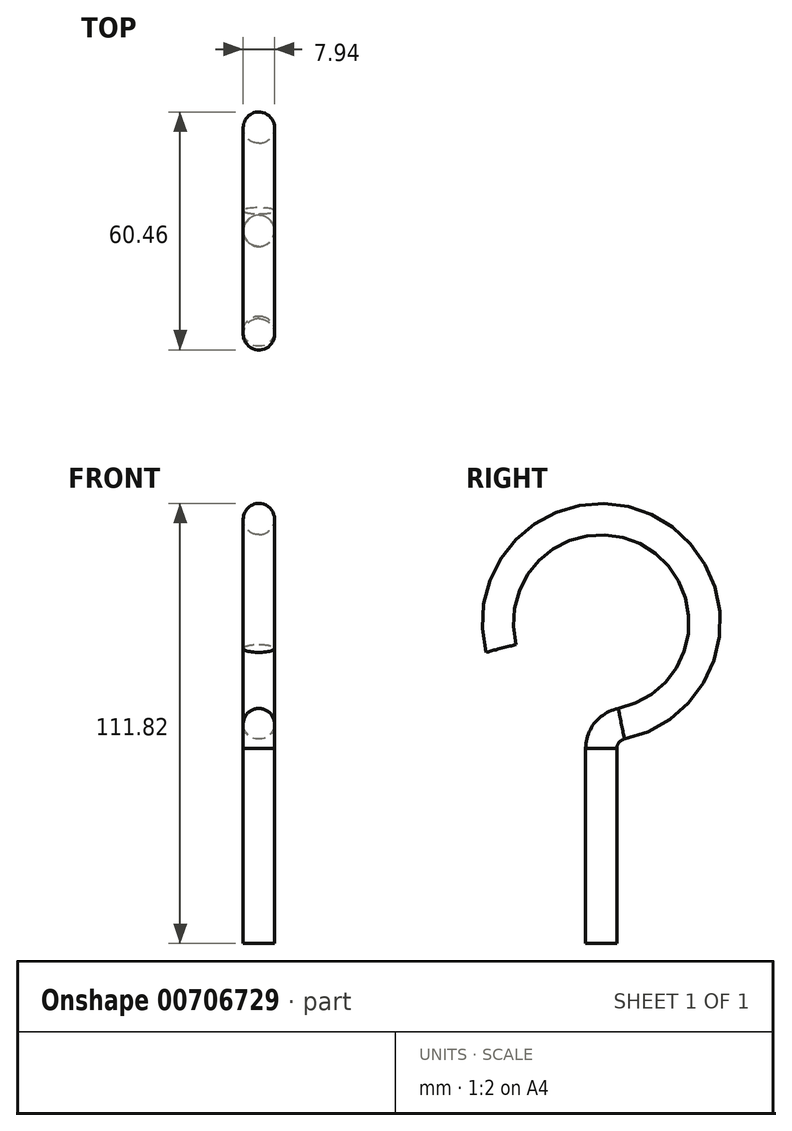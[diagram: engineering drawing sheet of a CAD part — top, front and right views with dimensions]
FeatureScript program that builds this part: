
annotation { "Feature Type Name" : "Feature", "Feature Type Description" : "" }
export const myFeature = defineFeature(function(context is Context, id is Id, definition is map)
    precondition{}
    {
        {
            var Q0;
            Q0=qCreatedBy(makeId("Right.planeOp"),FACE);
            var sketch = newSketch(context, id + "F0", { "sketchPlane" : qUnion([Q0])});
            skArc(sketch, "E0", {"start": v(5.1, 0.5) * mm, "mid": v(13.93, 48.52) * mm, "end": v(-25.46, 19.68) * mm});
            skPoint(sketch, "E0.first.point", {"position": v(0, 0) * mm});
            skPoint(sketch, "E0.second.point", {"position": v(0, 52.53) * mm});
            skPoint(sketch, "E0.third.point", {"position": v(-25.46, 19.68) * mm});
            skLineSegment(sketch, "E1", {"start": v(0, -5.72) * mm, "end": v(0, -55.31) * mm});
            skArc(sketch, "E2.filletArc", {"start": v(5.1, 0.5) * mm, "mid": v(1.44, -1.7) * mm, "end": v(0, -5.72) * mm});
            skSolve(sketch);
        }
        {
            var Q0;
            Q0=qCreatedBy(makeId("Front.planeOp"),FACE);
            var sketch = newSketch(context, id + "F1", { "sketchPlane" : qUnion([Q0])});
            skCircle(sketch, "E3", {"center": v(0, 52.53) * mm, "radius": 3.97 * mm});
            skSolve(sketch);
        }
        {
            var Q0;
            Q0 = qSketchRegion(id + "F0", true);
            var Q1;
            Q1=makeQuery(id+"F1.imprint","IMPRINT",FACE,{"disambiguationData":[TD([[makeQuery(id+"F1.imprint","IMPRINT",EDGE,{"derivedFrom":sQuery(id+"F1.wireOp",EDGE,"E3")}),1.0]])]});
            var Q2;
            Q2=sQuery(id+"F0.wireOp",EDGE,"E0");
            sweep(context, id + "F2", {"profiles" : qUnion([Q0, Q1]), "path" : qUnion([Q2])});
        }
        {
            var Q0;
            Q0=makeQuery(id+"F2.opSweep","CAP_FACE",FACE,{"disambiguationData":[OSD([sQuery(id+"F0.wireOp",VERTEX,"E0.start"),sQuery(id+"F1.wireOp",EDGE,"E3")])],"isStart":true});
            var Q1;
            Q1=makeQuery(id+"F2.opSweep","CAP_EDGE",EDGE,{"disambiguationData":[OSD([sQuery(id+"F0.wireOp",VERTEX,"E0.start"),sQuery(id+"F1.wireOp",EDGE,"E3")])],"isStart":true});
            var Q2;
            Q2=sQuery(id+"F0.wireOp",EDGE,"E2.filletArc");
            var Q3;
            Q3=sQuery(id+"F0.wireOp",EDGE,"E2.filletArc");
            sweep(context, id + "F3", {"profiles" : qUnion([Q0]), "surfaceProfiles" : qUnion([Q1, Q2]), "path" : qUnion([Q3])});
        }
        {
            var Q0;
            Q0=makeQuery(id+"F3.opSweep","CAP_FACE",FACE,{"disambiguationData":[OSD([sQuery(id+"F0.wireOp",VERTEX,"E0.start"),sQuery(id+"F0.wireOp",VERTEX,"E2.filletArc.end"),sQuery(id+"F1.wireOp",EDGE,"E3")])],"isStart":false});
            var Q1;
            Q1=sQuery(id+"F0.wireOp",EDGE,"E1");
            sweep(context, id + "F4", {"operationType" : NewBodyOperationType.ADD, "profiles" : qUnion([Q0]), "path" : qUnion([Q1])});
        }
    });
